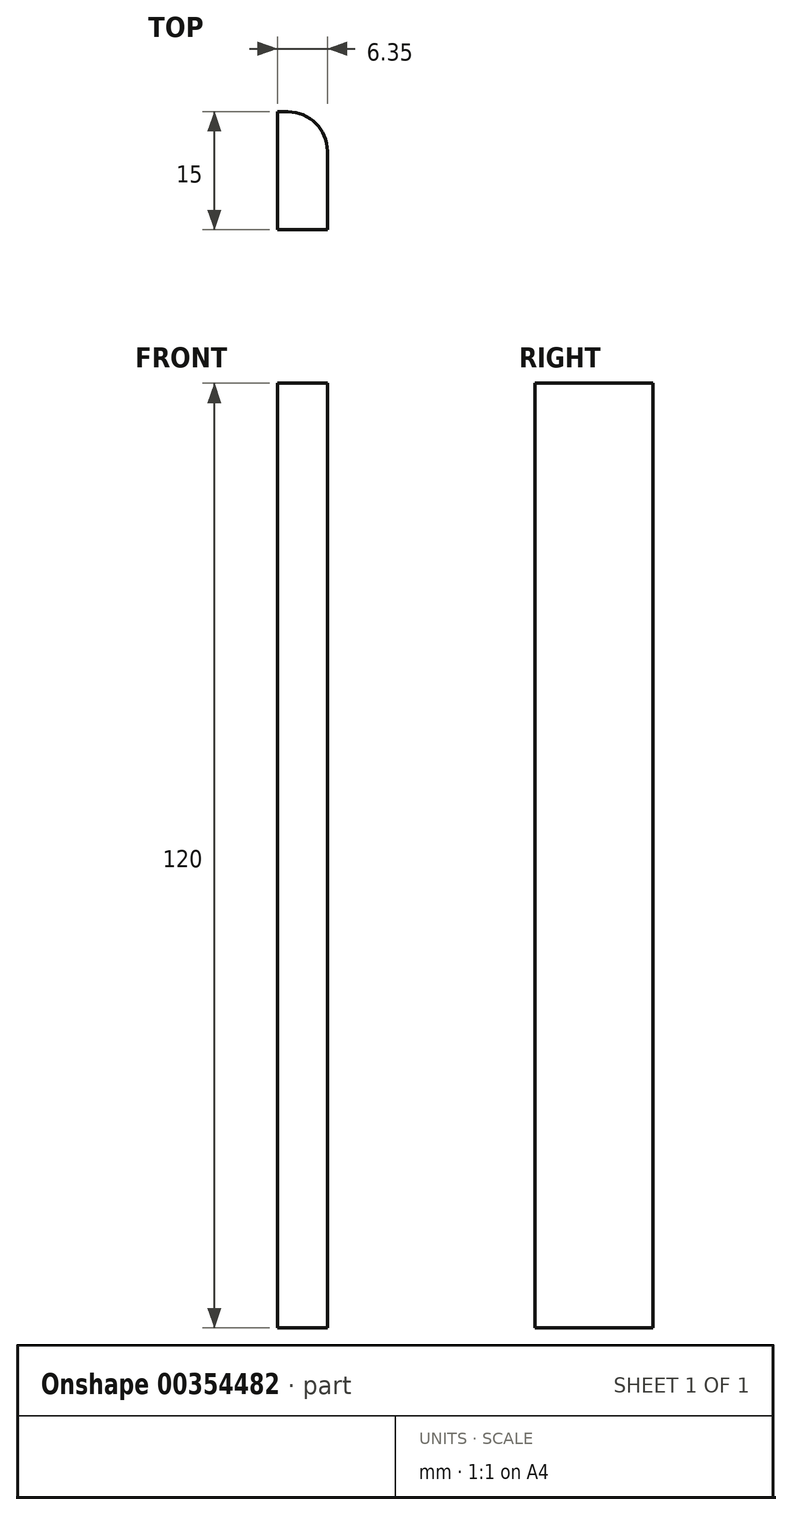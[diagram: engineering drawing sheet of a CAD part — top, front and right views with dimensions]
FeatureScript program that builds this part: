
annotation { "Feature Type Name" : "Feature", "Feature Type Description" : "" }
export const myFeature = defineFeature(function(context is Context, id is Id, definition is map)
    precondition{}
    {
        {
            var Q0;
            Q0=qCreatedBy(makeId("Top.planeOp"),FACE);
            var sketch = newSketch(context, id + "F0", { "sketchPlane" : qUnion([Q0])});
            skLineSegment(sketch, "E0.bottom", {"start": v(-9.26, 1.5) * mm, "end": v(-7.91, 1.5) * mm});
            skLineSegment(sketch, "E0.top", {"start": v(-9.26, -13.5) * mm, "end": v(-2.91, -13.5) * mm});
            skLineSegment(sketch, "E0.left", {"start": v(-9.26, 1.5) * mm, "end": v(-9.26, -13.5) * mm});
            skLineSegment(sketch, "E0.right", {"start": v(-2.91, -3.5) * mm, "end": v(-2.91, -13.5) * mm});
            skArc(sketch, "E1.filletArc", {"start": v(-2.91, -3.5) * mm, "mid": v(-4.38, 0.04) * mm, "end": v(-7.91, 1.5) * mm});
            skSolve(sketch);
        }
        {
            var Q0;
            Q0=makeQuery(id+"F0.imprint","IMPRINT",FACE,{"disambiguationData":[TD([[makeQuery(id+"F0.imprint","IMPRINT",EDGE,{"derivedFrom":sQuery(id+"F0.wireOp",EDGE,"E0.bottom")}),-1.0]])]});
            extrude(context, id + "F1", {"entities" : qUnion([Q0]), "depth" : 120 * mm});
        }
    });
